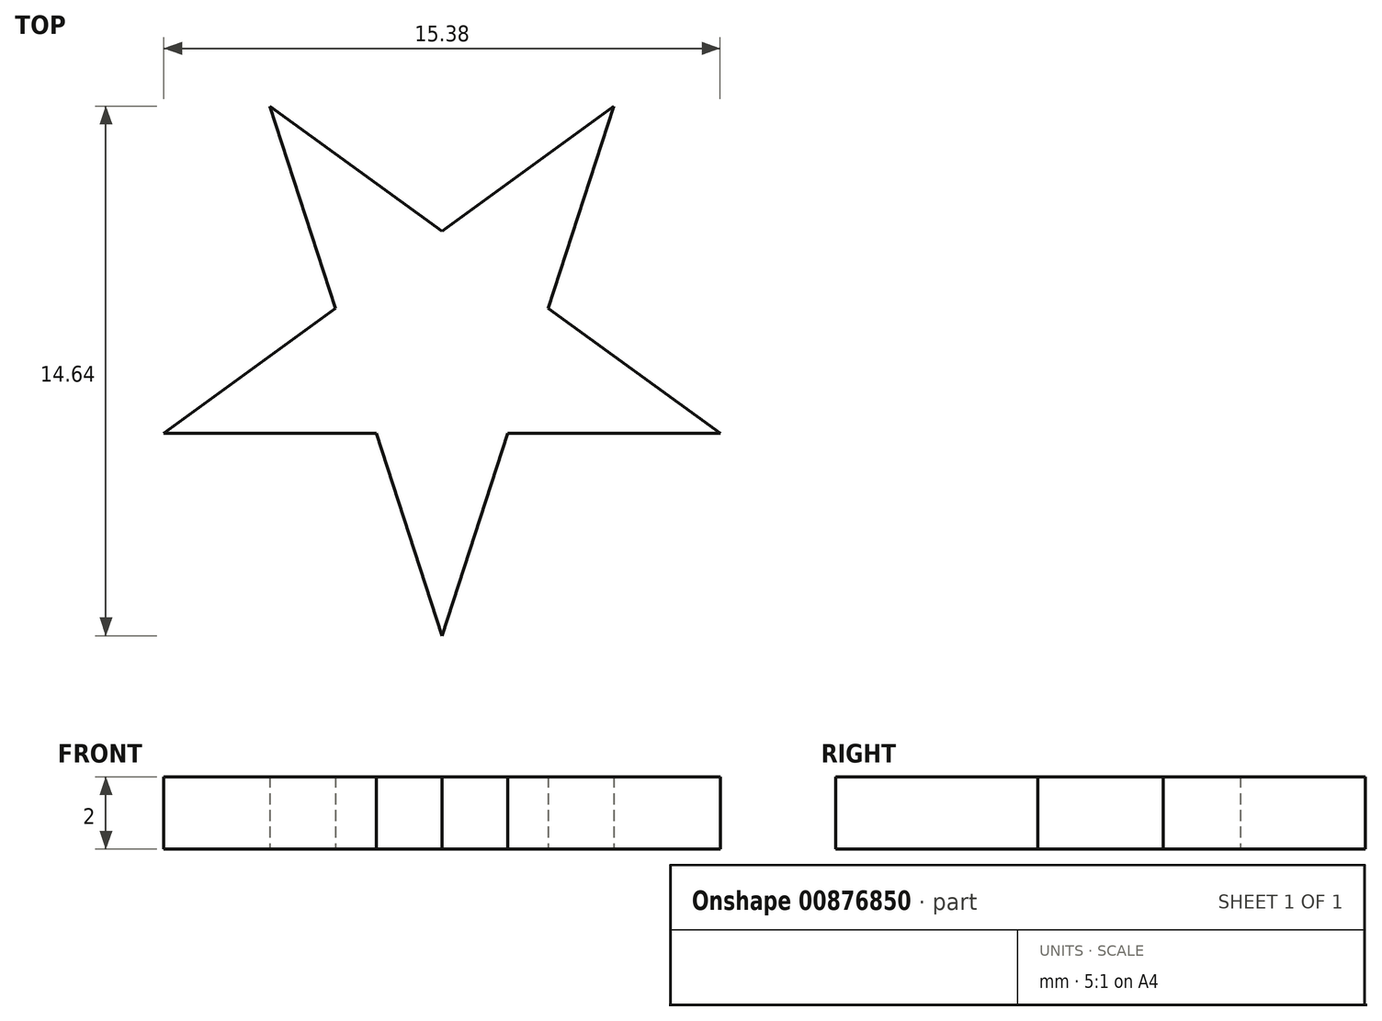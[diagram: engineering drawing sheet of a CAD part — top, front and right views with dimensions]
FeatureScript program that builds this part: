
annotation { "Feature Type Name" : "Feature", "Feature Type Description" : "" }
export const myFeature = defineFeature(function(context is Context, id is Id, definition is map)
    precondition{}
    {
        {
            var Q0;
            Q0=qCreatedBy(makeId("Top.planeOp"),FACE);
            var sketch = newSketch(context, id + "F0", { "sketchPlane" : qUnion([Q0])});
            skCircle(sketch, "E0.cCircle", {"center": v(0, 0) * mm, "radius": 2.5 * mm, "construction": true});
            skLineSegment(sketch, "E0.0", {"start": v(0, 3.1) * mm, "end": v(2.94, 0.95) * mm});
            skLineSegment(sketch, "E0.1", {"start": v(2.94, 0.95) * mm, "end": v(1.82, -2.5) * mm});
            skLineSegment(sketch, "E0.2", {"start": v(1.82, -2.5) * mm, "end": v(-1.82, -2.5) * mm});
            skLineSegment(sketch, "E0.3", {"start": v(-1.82, -2.5) * mm, "end": v(-2.94, 0.95) * mm});
            skLineSegment(sketch, "E0.4", {"start": v(-2.94, 0.95) * mm, "end": v(0, 3.1) * mm});
            skPoint(sketch, "E0.0.midPoint", {"position": v(1.47, 2.02) * mm});
            skLineSegment(sketch, "E1", {"start": v(2.38, -0.77) * mm, "end": v(7.7, -2.5) * mm});
            skLineSegment(sketch, "E2", {"start": v(1.82, -2.5) * mm, "end": v(7.7, -2.5) * mm});
            skLineSegment(sketch, "E3", {"start": v(2.94, 0.95) * mm, "end": v(7.7, -2.5) * mm});
            skLineSegment(sketch, "E4.1.0", {"start": v(0, 3.1) * mm, "end": v(4.76, 6.55) * mm});
            skLineSegment(sketch, "E4.1.1", {"start": v(2.94, 0.95) * mm, "end": v(4.76, 6.55) * mm});
            skLineSegment(sketch, "E4.2.0", {"start": v(-2.94, 0.95) * mm, "end": v(-4.76, 6.55) * mm});
            skLineSegment(sketch, "E4.2.1", {"start": v(0, 3.1) * mm, "end": v(-4.76, 6.55) * mm});
            skLineSegment(sketch, "E4.3.0", {"start": v(-1.82, -2.5) * mm, "end": v(-7.7, -2.5) * mm});
            skLineSegment(sketch, "E4.3.1", {"start": v(-2.94, 0.95) * mm, "end": v(-7.7, -2.5) * mm});
            skLineSegment(sketch, "E4.4.0", {"start": v(1.82, -2.5) * mm, "end": v(0, -8.1) * mm});
            skLineSegment(sketch, "E4.4.1", {"start": v(-1.82, -2.5) * mm, "end": v(0, -8.1) * mm});
            skSolve(sketch);
        }
        {
            var Q0;
            Q0=makeQuery(id+"F0.imprint","IMPRINT",FACE,{"disambiguationData":[TD([[makeQuery(id+"F0.imprint","IMPRINT",EDGE,{"derivedFrom":sQuery(id+"F0.wireOp",EDGE,"E0.4")}),1.0]])]});
            var Q1;
            Q1=makeQuery(id+"F0.imprint","IMPRINT",FACE,{"disambiguationData":[TD([[makeQuery(id+"F0.imprint","IMPRINT",EDGE,{"derivedFrom":sQuery(id+"F0.wireOp",EDGE,"E0.0")}),1.0]])]});
            var Q2;
            Q2=makeQuery(id+"F0.imprint","IMPRINT",FACE,{"disambiguationData":[TD([[makeQuery(id+"F0.imprint","IMPRINT",EDGE,{"derivedFrom":sQuery(id+"F0.wireOp",EDGE,"E0.0")}),-1.0]])]});
            var Q3;
            Q3=makeQuery(id+"F0.imprint","IMPRINT",FACE,{"disambiguationData":[TD([[makeQuery(id+"F0.imprint","IMPRINT",EDGE,{"derivedFrom":sQuery(id+"F0.wireOp",EDGE,"E0.3")}),1.0]])]});
            var Q4;
            {var subQ2=sQuery(id+"F0.wireOp",EDGE,"wUnIQyut-Jcoj-0Btm-gpiD-EEG1lG4h2nmR");Q4=makeQuery(id+"F0.imprint","IMPRINT",FACE,{"disambiguationData":[TD([[makeQuery(id+"F0.imprint","IMPRINT",EDGE,{"derivedFrom":subQ2}),-1.0]])]});}
            var Q5;
            Q5=makeQuery(id+"F0.imprint","IMPRINT",FACE,{"disambiguationData":[TD([[makeQuery(id+"F0.imprint","IMPRINT",EDGE,{"derivedFrom":sQuery(id+"F0.wireOp",EDGE,"E0.1")}),1.0]])]});
            var Q6;
            {var subQ2=sQuery(id+"F0.wireOp",EDGE,"wUnIQyut-Jcoj-0Btm-gpiD-EEG1lG4h2nmR");Q6=makeQuery(id+"F0.imprint","IMPRINT",FACE,{"disambiguationData":[TD([[makeQuery(id+"F0.imprint","IMPRINT",EDGE,{"derivedFrom":subQ2}),1.0]])]});}
            var Q7;
            Q7=makeQuery(id+"F0.imprint","IMPRINT",FACE,{"disambiguationData":[TD([[makeQuery(id+"F0.imprint","IMPRINT",EDGE,{"derivedFrom":sQuery(id+"F0.wireOp",EDGE,"E0.2")}),1.0]])]});
            extrude(context, id + "F1", {"entities" : qUnion([Q0, Q1, Q2, Q3, Q4, Q5, Q6, Q7]), "depth" : 2 * mm, "offsetDistance" : 25 * mm});
        }
    });
